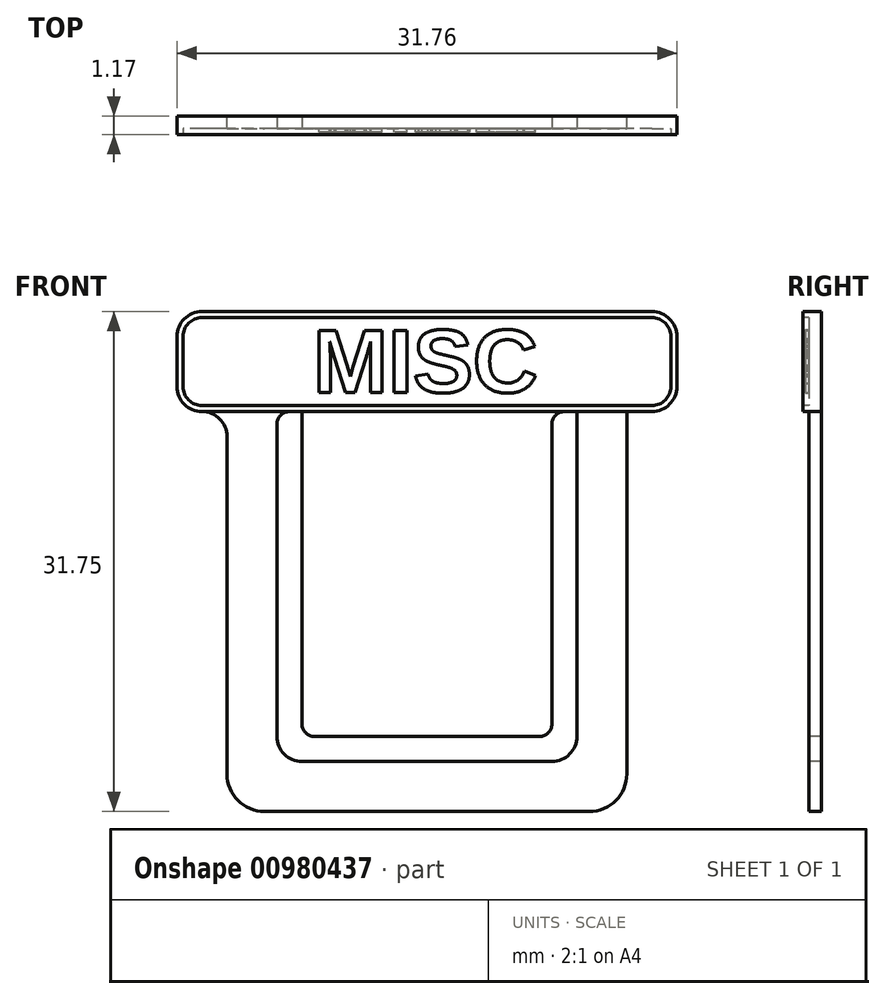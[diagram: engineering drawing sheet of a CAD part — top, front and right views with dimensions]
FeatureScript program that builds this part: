
annotation { "Feature Type Name" : "Feature", "Feature Type Description" : "" }
export const myFeature = defineFeature(function(context is Context, id is Id, definition is map)
    precondition{}
    {
        {
            var Q0;
            Q0=qCreatedBy(makeId("Front.planeOp"),FACE);
            var sketch = newSketch(context, id + "F0", { "sketchPlane" : qUnion([Q0])});
            skLineSegment(sketch, "E0.bottom", {"start": v(12.7, 12.7) * mm, "end": v(-12.7, 12.7) * mm});
            skLineSegment(sketch, "E0.top", {"start": v(12.7, -12.7) * mm, "end": v(-12.7, -12.7) * mm});
            skLineSegment(sketch, "E0.left", {"start": v(12.7, 12.7) * mm, "end": v(12.7, -12.7) * mm});
            skLineSegment(sketch, "E0.right", {"start": v(-12.7, 12.7) * mm, "end": v(-12.7, -12.7) * mm});
            skPoint(sketch, "E0.middle", {"position": v(0, 0) * mm});
            skSolve(sketch);
        }
        {
            var Q0;
            Q0=makeQuery(id+"F0.imprint","IMPRINT",FACE,{"disambiguationData":[TD([[makeQuery(id+"F0.imprint","IMPRINT",EDGE,{"derivedFrom":sQuery(id+"F0.wireOp",EDGE,"E0.bottom")}),1.0]])]});
            extrude(context, id + "F1", {"entities" : qUnion([Q0]), "depth" : 0.8 * mm, "offsetDistance" : 25.4 * mm});
        }
        {
            var Q0;
            Q0=makeQuery(id+"F1.opExtrude","SWEPT_EDGE",EDGE,{"disambiguationData":[OSD([sQuery(id+"F0.wireOp",EDGE,"E0.top"),sQuery(id+"F0.wireOp",EDGE,"E0.left")])]});
            var Q1;
            Q1=makeQuery(id+"F1.opExtrude","SWEPT_EDGE",EDGE,{"disambiguationData":[OSD([sQuery(id+"F0.wireOp",EDGE,"E0.top"),sQuery(id+"F0.wireOp",EDGE,"E0.right")])]});
            fillet(context, id + "F2", {"entities" : qUnion([Q0, Q1]), "radius" : 2.38 * mm, "tangentPropagation" : true, "allowEdgeOverflow" : false});
        }
        {
            var Q0;
            Q0=makeQuery(id+"F1.opExtrude","CAP_FACE",FACE,{"disambiguationData":[OSD([sQuery(id+"F0.wireOp",EDGE,"E0.bottom"),sQuery(id+"F0.wireOp",EDGE,"E0.top"),sQuery(id+"F0.wireOp",EDGE,"E0.left"),sQuery(id+"F0.wireOp",EDGE,"E0.right")])],"isStart":false});
            var sketch = newSketch(context, id + "F3", { "sketchPlane" : qUnion([Q0])});
            skLineSegment(sketch, "E1.bottom", {"start": v(9.52, 12.7) * mm, "end": v(-9.53, 12.7) * mm});
            skLineSegment(sketch, "E1.top", {"start": v(9.53, -9.53) * mm, "end": v(-9.52, -9.53) * mm});
            skLineSegment(sketch, "E1.left", {"start": v(9.52, 12.7) * mm, "end": v(9.53, -9.53) * mm});
            skLineSegment(sketch, "E1.right", {"start": v(-9.53, 12.7) * mm, "end": v(-9.52, -9.53) * mm});
            skPoint(sketch, "E1.middle", {"position": v(0, 0) * mm});
            skSolve(sketch);
        }
        {
            var Q0;
            Q0=makeQuery(id+"F3.imprint","IMPRINT",FACE,{"disambiguationData":[TD([[makeQuery(id+"F3.imprint","IMPRINT",EDGE,{"derivedFrom":sQuery(id+"F3.wireOp",EDGE,"E1.bottom")}),1.0]])]});
            extrude(context, id + "F4", {"entities" : qUnion([Q0]), "operationType" : NewBodyOperationType.REMOVE, "oppositeDirection" : true, "depth" : 4.93 * mm, "offsetDistance" : 25.4 * mm});
        }
        {
            var Q0;
            Q0=makeQuery(id+"F1.opExtrude","CAP_FACE",FACE,{"disambiguationData":[OSD([sQuery(id+"F0.wireOp",EDGE,"E0.bottom"),sQuery(id+"F0.wireOp",EDGE,"E0.top"),sQuery(id+"F0.wireOp",EDGE,"E0.left"),sQuery(id+"F0.wireOp",EDGE,"E0.right")])],"isStart":false});
            var sketch = newSketch(context, id + "F5", { "sketchPlane" : qUnion([Q0])});
            skLineSegment(sketch, "E2.bottom", {"start": v(-15.88, 12.7) * mm, "end": v(15.88, 12.7) * mm});
            skLineSegment(sketch, "E2.top", {"start": v(-15.88, 19.05) * mm, "end": v(15.88, 19.05) * mm});
            skLineSegment(sketch, "E2.left", {"start": v(-15.88, 12.7) * mm, "end": v(-15.88, 19.05) * mm});
            skLineSegment(sketch, "E2.right", {"start": v(15.87, 12.7) * mm, "end": v(15.87, 19.05) * mm});
            skSolve(sketch);
        }
        {
            var Q0;
            Q0=makeQuery(id+"F5.imprint","IMPRINT",FACE,{"disambiguationData":[TD([[makeQuery(id+"F5.imprint","IMPRINT",EDGE,{"derivedFrom":sQuery(id+"F5.wireOp",EDGE,"E2.top")}),-1.0]])]});
            extrude(context, id + "F6", {"entities" : qUnion([Q0]), "operationType" : NewBodyOperationType.ADD, "oppositeDirection" : true, "depth" : 0.8 * mm, "offsetDistance" : 25.4 * mm});
        }
        {
            var Q0;
            Q0=makeQuery(id+"F6.opExtrude","SWEPT_EDGE",EDGE,{"disambiguationData":[OSD([sQuery(id+"F5.wireOp",EDGE,"E2.top"),sQuery(id+"F5.wireOp",EDGE,"E2.left")])]});
            var Q1;
            Q1=makeQuery(id+"F6.opExtrude","SWEPT_EDGE",EDGE,{"disambiguationData":[OSD([sQuery(id+"F5.wireOp",EDGE,"E2.top"),sQuery(id+"F5.wireOp",EDGE,"E2.right")])]});
            var Q2;
            Q2=makeQuery(id+"F6.opExtrude","SWEPT_EDGE",EDGE,{"disambiguationData":[OSD([sQuery(id+"F5.wireOp",EDGE,"E2.bottom"),sQuery(id+"F5.wireOp",EDGE,"E2.right")])]});
            var Q3;
            Q3=makeQuery(id+"F1.opExtrude","SWEPT_EDGE",EDGE,{"disambiguationData":[OSD([sQuery(id+"F0.wireOp",EDGE,"E0.bottom"),sQuery(id+"F0.wireOp",EDGE,"E0.left")])]});
            var Q4;
            Q4=makeQuery(id+"F6.opExtrude","SWEPT_EDGE",EDGE,{"disambiguationData":[OSD([sQuery(id+"F5.wireOp",EDGE,"E2.bottom"),sQuery(id+"F5.wireOp",EDGE,"E2.left")])]});
            var Q5;
            Q5=makeQuery(id+"F1.opExtrude","SWEPT_EDGE",EDGE,{"disambiguationData":[OSD([sQuery(id+"F0.wireOp",EDGE,"E0.bottom"),sQuery(id+"F0.wireOp",EDGE,"E0.right")])]});
            fillet(context, id + "F7", {"entities" : qUnion([Q0, Q1, Q2, Q3, Q4, Q5]), "radius" : 1.59 * mm, "tangentPropagation" : true, "allowEdgeOverflow" : false});
        }
        {
            var Q0;
            Q0=makeQuery(id+"F4.boolean.opBoolean","COPY",EDGE,{"derivedFrom":makeQuery(id+"F4.opExtrude","SWEPT_EDGE",EDGE,{"disambiguationData":[OSD([sQuery(id+"F3.wireOp",EDGE,"E1.top"),sQuery(id+"F3.wireOp",EDGE,"E1.right")])]})});
            var Q1;
            Q1=makeQuery(id+"F4.boolean.opBoolean","COPY",EDGE,{"derivedFrom":makeQuery(id+"F4.opExtrude","SWEPT_EDGE",EDGE,{"disambiguationData":[OSD([sQuery(id+"F3.wireOp",EDGE,"E1.top"),sQuery(id+"F3.wireOp",EDGE,"E1.left")])]})});
            fillet(context, id + "F8", {"entities" : qUnion([Q0, Q1]), "radius" : 1.59 * mm, "tangentPropagation" : true, "allowEdgeOverflow" : false});
        }
        {
            var Q0;
            Q0=makeQuery(id+"F6.boolean.opBoolean","MERGE",FACE,{"derivedFrom":[makeQuery(id+"F1.opExtrude","CAP_FACE",FACE,{"disambiguationData":[OSD([sQuery(id+"F0.wireOp",EDGE,"E0.bottom"),sQuery(id+"F0.wireOp",EDGE,"E0.top"),sQuery(id+"F0.wireOp",EDGE,"E0.left"),sQuery(id+"F0.wireOp",EDGE,"E0.right")])],"isStart":false}),makeQuery(id+"F6.opExtrude","CAP_FACE",FACE,{"disambiguationData":[OSD([sQuery(id+"F5.wireOp",EDGE,"E2.bottom"),sQuery(id+"F5.wireOp",EDGE,"E2.top"),sQuery(id+"F5.wireOp",EDGE,"E2.left"),sQuery(id+"F5.wireOp",EDGE,"E2.right")])],"isStart":true})]});
            var sketch = newSketch(context, id + "F9", { "sketchPlane" : qUnion([Q0])});
            skLineSegment(sketch, "E3.bottom", {"start": v(-7.94, 12.7) * mm, "end": v(7.94, 12.7) * mm});
            skLineSegment(sketch, "E3.top", {"start": v(-7.94, -7.94) * mm, "end": v(7.94, -7.94) * mm});
            skLineSegment(sketch, "E3.left", {"start": v(-7.94, 12.7) * mm, "end": v(-7.94, -7.94) * mm});
            skLineSegment(sketch, "E3.right", {"start": v(7.94, 12.7) * mm, "end": v(7.94, -7.94) * mm});
            skSolve(sketch);
        }
        {
            var Q0;
            Q0=makeQuery(id+"F9.imprint","IMPRINT",FACE,{"disambiguationData":[TD([[makeQuery(id+"F9.imprint","IMPRINT",EDGE,{"derivedFrom":sQuery(id+"F9.wireOp",EDGE,"E3.bottom")}),1.0]])]});
            extrude(context, id + "F10", {"entities" : qUnion([Q0]), "operationType" : NewBodyOperationType.ADD, "oppositeDirection" : true, "depth" : 0.8 * mm, "offsetDistance" : 25.4 * mm});
        }
        {
            var Q0;
            Q0=makeQuery(id+"F10.opExtrude","SWEPT_EDGE",EDGE,{"disambiguationData":[OSD([sQuery(id+"F5.wireOp",EDGE,"E2.bottom"),sQuery(id+"F9.wireOp",EDGE,"E3.bottom"),sQuery(id+"F9.wireOp",EDGE,"E3.left")])]});
            var Q1;
            Q1=makeQuery(id+"F4.boolean.opBoolean","COPY",EDGE,{"derivedFrom":makeQuery(id+"F4.opExtrude","SWEPT_EDGE",EDGE,{"disambiguationData":[OSD([sQuery(id+"F0.wireOp",EDGE,"E0.bottom"),sQuery(id+"F3.wireOp",EDGE,"E1.bottom"),sQuery(id+"F3.wireOp",EDGE,"E1.right")])]})});
            var Q2;
            Q2=makeQuery(id+"F10.opExtrude","SWEPT_EDGE",EDGE,{"disambiguationData":[OSD([sQuery(id+"F5.wireOp",EDGE,"E2.bottom"),sQuery(id+"F9.wireOp",EDGE,"E3.bottom"),sQuery(id+"F9.wireOp",EDGE,"E3.right")])]});
            var Q3;
            Q3=makeQuery(id+"F4.boolean.opBoolean","COPY",EDGE,{"derivedFrom":makeQuery(id+"F4.opExtrude","SWEPT_EDGE",EDGE,{"disambiguationData":[OSD([sQuery(id+"F0.wireOp",EDGE,"E0.bottom"),sQuery(id+"F3.wireOp",EDGE,"E1.bottom"),sQuery(id+"F3.wireOp",EDGE,"E1.left")])]})});
            fillet(context, id + "F11", {"entities" : qUnion([Q0, Q1, Q2, Q3]), "radius" : 0.8 * mm, "tangentPropagation" : true, "allowEdgeOverflow" : false});
        }
        {
            var Q0;
            Q0=makeQuery(id+"F10.opExtrude","SWEPT_EDGE",EDGE,{"disambiguationData":[OSD([sQuery(id+"F9.wireOp",EDGE,"E3.top"),sQuery(id+"F9.wireOp",EDGE,"E3.left")])]});
            var Q1;
            Q1=makeQuery(id+"F10.opExtrude","SWEPT_EDGE",EDGE,{"disambiguationData":[OSD([sQuery(id+"F9.wireOp",EDGE,"E3.top"),sQuery(id+"F9.wireOp",EDGE,"E3.right")])]});
            fillet(context, id + "F12", {"entities" : qUnion([Q0, Q1]), "radius" : 0.8 * mm, "tangentPropagation" : true, "allowEdgeOverflow" : false});
        }
        {
            var Q0;
            Q0=makeQuery(id+"F10.boolean.opBoolean","MERGE",FACE,{"derivedFrom":[makeQuery(id+"F6.boolean.opBoolean","MERGE",FACE,{"derivedFrom":[makeQuery(id+"F1.opExtrude","CAP_FACE",FACE,{"disambiguationData":[OSD([sQuery(id+"F0.wireOp",EDGE,"E0.bottom"),sQuery(id+"F0.wireOp",EDGE,"E0.top"),sQuery(id+"F0.wireOp",EDGE,"E0.left"),sQuery(id+"F0.wireOp",EDGE,"E0.right")])],"isStart":false}),makeQuery(id+"F6.opExtrude","CAP_FACE",FACE,{"disambiguationData":[OSD([sQuery(id+"F5.wireOp",EDGE,"E2.bottom"),sQuery(id+"F5.wireOp",EDGE,"E2.top"),sQuery(id+"F5.wireOp",EDGE,"E2.left"),sQuery(id+"F5.wireOp",EDGE,"E2.right")])],"isStart":true})]}),makeQuery(id+"F10.opExtrude","CAP_FACE",FACE,{"disambiguationData":[OSD([sQuery(id+"F9.wireOp",EDGE,"E3.bottom"),sQuery(id+"F9.wireOp",EDGE,"E3.top"),sQuery(id+"F9.wireOp",EDGE,"E3.left"),sQuery(id+"F9.wireOp",EDGE,"E3.right")])],"isStart":true})]});
            var sketch = newSketch(context, id + "F13", { "sketchPlane" : qUnion([Q0])});
            skArc(sketch, "E4.0", {"start": v(-14.29, 19.05) * mm, "mid": v(-15.41, 18.59) * mm, "end": v(-15.88, 17.46) * mm});
            skLineSegment(sketch, "E5.0", {"start": v(-15.88, 14.29) * mm, "end": v(-15.88, 17.46) * mm});
            skArc(sketch, "E6.0", {"start": v(-15.88, 14.29) * mm, "mid": v(-15.41, 13.16) * mm, "end": v(-14.29, 12.7) * mm});
            skLineSegment(sketch, "E7.0", {"start": v(-14.29, 19.05) * mm, "end": v(14.29, 19.05) * mm});
            skArc(sketch, "E8.0", {"start": v(15.87, 17.46) * mm, "mid": v(15.41, 18.59) * mm, "end": v(14.29, 19.05) * mm});
            skLineSegment(sketch, "E9.0", {"start": v(15.87, 14.29) * mm, "end": v(15.87, 17.46) * mm});
            skArc(sketch, "E10.0", {"start": v(14.29, 12.7) * mm, "mid": v(15.41, 13.16) * mm, "end": v(15.87, 14.29) * mm});
            skLineSegment(sketch, "E11", {"start": v(-14.29, 12.7) * mm, "end": v(14.29, 12.7) * mm});
            skSolve(sketch);
        }
        {
            var Q0;
            Q0=makeQuery(id+"F13.imprint","IMPRINT",FACE,{"disambiguationData":[TD([[makeQuery(id+"F13.imprint","IMPRINT",EDGE,{"derivedFrom":sQuery(id+"F13.wireOp",EDGE,"E4.0")}),1.0]])]});
            extrude(context, id + "F14", {"entities" : qUnion([Q0]), "operationType" : NewBodyOperationType.ADD, "depth" : 0.38 * mm, "offsetDistance" : 25.4 * mm});
        }
        {
            var Q0;
            Q0=makeQuery(id+"F14.opExtrude","CAP_FACE",FACE,{"disambiguationData":[OSD([sQuery(id+"F13.wireOp",EDGE,"E4.0"),sQuery(id+"F13.wireOp",EDGE,"E5.0"),sQuery(id+"F13.wireOp",EDGE,"E6.0"),sQuery(id+"F13.wireOp",EDGE,"E7.0"),sQuery(id+"F13.wireOp",EDGE,"E8.0"),sQuery(id+"F13.wireOp",EDGE,"E9.0"),sQuery(id+"F13.wireOp",EDGE,"E10.0"),sQuery(id+"F13.wireOp",EDGE,"E11")])],"isStart":false});
            var sketch = newSketch(context, id + "F15", { "sketchPlane" : qUnion([Q0])});
            skArc(sketch, "E12.0", {"start": v(-14.29, 19.05) * mm, "mid": v(-15.41, 18.59) * mm, "end": v(-15.88, 17.46) * mm});
            skLineSegment(sketch, "E13.0", {"start": v(-14.29, 19.05) * mm, "end": v(14.29, 19.05) * mm});
            skLineSegment(sketch, "E14.0", {"start": v(-15.88, 14.29) * mm, "end": v(-15.88, 17.46) * mm});
            skArc(sketch, "E15.0", {"start": v(-15.88, 14.29) * mm, "mid": v(-15.41, 13.16) * mm, "end": v(-14.29, 12.7) * mm});
            skLineSegment(sketch, "E16.0", {"start": v(-14.29, 12.7) * mm, "end": v(14.29, 12.7) * mm});
            skArc(sketch, "E17.0", {"start": v(14.29, 12.7) * mm, "mid": v(15.41, 13.16) * mm, "end": v(15.87, 14.29) * mm});
            skArc(sketch, "E18.0", {"start": v(15.87, 17.46) * mm, "mid": v(15.41, 18.59) * mm, "end": v(14.29, 19.05) * mm});
            skArc(sketch, "E19", {"start": v(-14.29, 18.67) * mm, "mid": v(-15.14, 18.32) * mm, "end": v(-15.5, 17.46) * mm});
            skArc(sketch, "E20", {"start": v(-15.5, 14.29) * mm, "mid": v(-15.14, 13.43) * mm, "end": v(-14.29, 13.08) * mm});
            skArc(sketch, "E21", {"start": v(15.5, 17.46) * mm, "mid": v(15.14, 18.32) * mm, "end": v(14.29, 18.67) * mm});
            skArc(sketch, "E22", {"start": v(14.29, 13.08) * mm, "mid": v(15.14, 13.43) * mm, "end": v(15.5, 14.29) * mm});
            skLineSegment(sketch, "E23", {"start": v(-14.29, 19.05) * mm, "end": v(-14.29, 12.7) * mm, "construction": true});
            skLineSegment(sketch, "E24", {"start": v(-15.88, 17.46) * mm, "end": v(15.87, 17.46) * mm, "construction": true});
            skLineSegment(sketch, "E25", {"start": v(14.29, 19.05) * mm, "end": v(14.29, 12.7) * mm, "construction": true});
            skLineSegment(sketch, "E26", {"start": v(15.87, 14.29) * mm, "end": v(-15.88, 14.29) * mm, "construction": true});
            skLineSegment(sketch, "E27", {"start": v(14.29, 18.67) * mm, "end": v(-14.29, 18.67) * mm});
            skLineSegment(sketch, "E28", {"start": v(-15.5, 17.46) * mm, "end": v(-15.5, 14.29) * mm});
            skLineSegment(sketch, "E29", {"start": v(-14.29, 13.08) * mm, "end": v(14.29, 13.08) * mm});
            skLineSegment(sketch, "E30", {"start": v(15.5, 17.46) * mm, "end": v(15.5, 14.29) * mm});
            skSolve(sketch);
        }
        {
            var Q0;
            Q0=makeQuery(id+"F15.imprint","IMPRINT",FACE,{"disambiguationData":[TD([[makeQuery(id+"F15.imprint","IMPRINT",EDGE,{"derivedFrom":sQuery(id+"F15.wireOp",EDGE,"E19")}),1.0]])]});
            var Q1;
            {var subQ0=sQuery(id+"F9.wireOp",EDGE,"E3.right");var subQ1=sQuery(id+"F9.wireOp",EDGE,"E3.top");var subQ3=sQuery(id+"F0.wireOp",EDGE,"E0.bottom");var subQ4=sQuery(id+"F9.wireOp",EDGE,"E3.left");var subQ5=makeQuery(id+"F6.opExtrude","CAP_FACE",FACE,{"disambiguationData":[OSD([sQuery(id+"F5.wireOp",EDGE,"E2.bottom"),sQuery(id+"F5.wireOp",EDGE,"E2.top"),sQuery(id+"F5.wireOp",EDGE,"E2.left"),sQuery(id+"F5.wireOp",EDGE,"E2.right")])],"isStart":true});var subQ6=makeQuery(id+"F1.opExtrude","CAP_FACE",FACE,{"disambiguationData":[OSD([subQ3,sQuery(id+"F0.wireOp",EDGE,"E0.top"),sQuery(id+"F0.wireOp",EDGE,"E0.left"),sQuery(id+"F0.wireOp",EDGE,"E0.right")])],"isStart":false});var subQ7=makeQuery(id+"F10.opExtrude","CAP_FACE",FACE,{"disambiguationData":[OSD([sQuery(id+"F9.wireOp",EDGE,"E3.bottom"),subQ1,subQ4,subQ0])],"isStart":true});Q1=makeQuery(id+"F14.boolean.opBoolean","SPLIT",FACE,{"disambiguationData":[TD([makeQuery(id+"F10.opExtrude","SWEPT_FACE",FACE,{"disambiguationData":[OSD([subQ1])]})])],"derivedFrom":makeQuery(id+"F10.boolean.opBoolean","MERGE",FACE,{"derivedFrom":[makeQuery(id+"F6.boolean.opBoolean","MERGE",FACE,{"derivedFrom":[subQ6,subQ5]}),subQ7]})});}
            extrude(context, id + "F16", {"entities" : qUnion([Q0]), "operationType" : NewBodyOperationType.REMOVE, "endBound" : BoundingType.UP_TO_SURFACE, "oppositeDirection" : true, "depth" : 25.4 * mm, "endBoundEntityFace" : qUnion([Q1]), "offsetDistance" : 25.4 * mm});
        }
        {
            var Q0;
            Q0=qCreatedBy(makeId("Front.planeOp"),FACE);
            var sketch = newSketch(context, id + "F17", { "sketchPlane" : qUnion([Q0])});
            skText(sketch, "E31", { "text": "MISC", "fontName": "Arimo-Bold.ttf"});
            const initialGuessF17  = {"E31": [-0.00725, 0.01392, 1, 0, 0.00412]};
            skSetInitialGuess(sketch, initialGuessF17);
            skSolve(sketch);
        }
        {
            var Q0;
            Q0=qSketchRegion(id+"F17",true);
            extrude(context, id + "F18", {"entities" : qUnion([Q0]), "operationType" : NewBodyOperationType.ADD, "depth" : 1.02 * mm, "offsetDistance" : 25.4 * mm});
        }
    });
